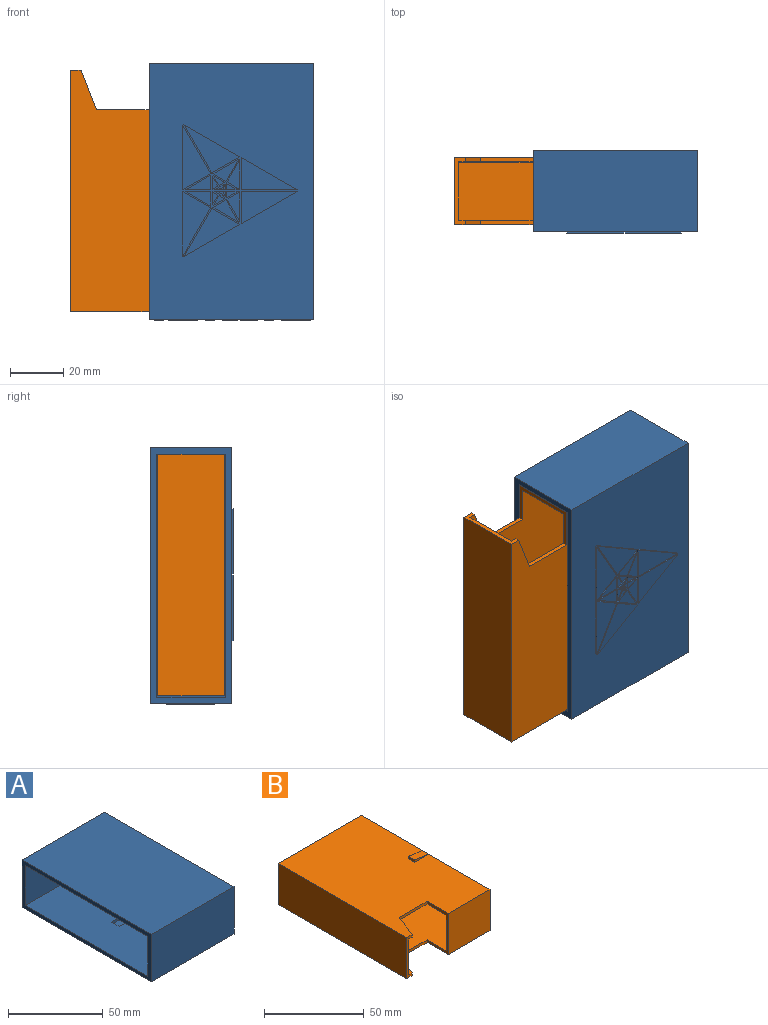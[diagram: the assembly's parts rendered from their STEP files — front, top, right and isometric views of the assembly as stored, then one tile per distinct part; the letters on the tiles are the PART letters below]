
ASSEMBLY  parts=2 mates=1
PART A: 220 faces, bbox 61.9x96.7x31.3 mm
  f0: plane 61.9x30.6mm, normal (0,1,0), area 1621.7mm2, adj f1,f2,f5,f7,f123,f124,f125,f126
  f1: plane 96.6x61.9mm, normal (0,0,-1), area 5003.8mm2, adj f0,f2,f5,f6,f27,f28,f29,f31
  f2: plane 96.6x30.6mm, normal (1,0,0), area 2577.4mm2, adj f0,f1,f6,f7,f19,f20,f21,f22
  f3: plane 91.8x59.5mm, normal (0,0,1), area 5249.3mm2, adj f5,f8,f9,f10,f15,f17,f18
  f4: plane 91.8x59.5mm, normal (0,0,-1), area 5249.3mm2, adj f5,f8,f9,f10,f11,f12,f13
  f5: plane 96.6x30.6mm, normal (-1,0,0), area 587.5mm2, adj f0,f1,f3,f4,f6,f7,f8,f9
  f6: plane 61.9x30.6mm, normal (0,-1,0), area 1894.1mm2, adj f1,f2,f5,f7
  f7: plane 96.6x61.9mm, normal (0,0,1), area 5979.5mm2, adj f0,f2,f5,f6
  f8: plane 59.5x25.8mm, normal (0,-1,0), area 1535.1mm2, adj f3,f4,f5,f10
  f9: plane 59.5x25.8mm, normal (0,1,0), area 1535.1mm2, adj f3,f4,f5,f10
  f10: plane 91.8x28.8mm, normal (-1,0,0), area 2006.7mm2, adj f3,f4,f8,f9,f11,f12,f14,f15
  f11: plane 38x1.5mm, normal (0,-1,0), area 57mm2, adj f4,f10,f13,f14
  f12: plane 38x1.5mm, normal (0,1,0), area 57mm2, adj f4,f10,f13,f14
  f13: plane 5.6x1.5mm, normal (1,0,0), area 8.4mm2, adj f4,f11,f12,f14
  f14: plane 38x5.6mm, normal (0,0,-1), area 212.8mm2, adj f10,f11,f12,f13
  f15: plane 38x1.5mm, normal (0,-1,0), area 57mm2, adj f3,f10,f16,f18
  f16: plane 38x5.6mm, normal (0,0,1), area 212.8mm2, adj f10,f15,f17,f18
  f17: plane 38x1.5mm, normal (0,1,0), area 57mm2, adj f3,f10,f16,f18
  f18: plane 5.6x1.5mm, normal (1,0,0), area 8.4mm2, adj f3,f15,f16,f17
  f19: plane 10x2.4mm, normal (0,0,1), area 24mm2, adj f2,f10,f24,f25
  f20: plane 10x2.4mm, normal (0,1,0), area 24mm2, adj f2,f10,f25,f26
  f21: plane 10x2.4mm, normal (0,0,-1), area 24mm2, adj f2,f10,f23,f26
  f22: plane 10x2.4mm, normal (0,-1,0), area 24mm2, adj f2,f10,f23,f24
  f23: cylinder r=5mm len=5mm, axis (-1,0,0), area 18.8mm2, adj f2,f10,f21,f22
  f24: cylinder r=5mm len=5mm, axis (1,0,0), area 18.8mm2, adj f2,f10,f19,f22
  f25: cylinder r=5mm len=5mm, axis (-1,0,0), area 18.8mm2, adj f2,f10,f19,f20
  f26: cylinder r=5mm len=5mm, axis (1,0,0), area 18.8mm2, adj f2,f10,f20,f21
  f27: plane 24.4x0.67mm, normal (-1,0,0), area 16.3mm2, adj f1,f28,f29,f30
  f28: plane 18.3x10.57mm, normal (0.87,0.5,0), area 14.1mm2, adj f1,f27,f29,f30
  f29: plane 10.57x6.1mm, normal (0.5,-0.87,0), area 8.1mm2, adj f1,f27,f28,f30
  f30: plane 24.4x10.57mm, normal (0,0,-1), area 128.9mm2, adj f27,f28,f29
  f31: plane 24.4x0.67mm, normal (-1,0,0), area 16.3mm2, adj f1,f32,f33,f34
  f32: plane 10.57x6.1mm, normal (0.5,0.87,0), area 8.1mm2, adj f1,f31,f33,f34
  f33: plane 18.3x10.57mm, normal (0.87,-0.5,0), area 14.1mm2, adj f1,f31,f32,f34
  f34: plane 24.4x10.57mm, normal (0,0,-1), area 128.9mm2, adj f31,f32,f33
  f35: plane 10.57x6.1mm, normal (0.5,0.87,0), area 8.1mm2, adj f1,f36,f37,f38
  f36: plane 21.13x12.2mm, normal (0.5,-0.87,0), area 16.3mm2, adj f1,f35,f37,f38
  f37: plane 18.3x10.57mm, normal (-0.87,0.5,0), area 14.1mm2, adj f1,f35,f36,f38
  f38: plane 21.13x18.3mm, normal (0,0,-1), area 128.9mm2, adj f35,f36,f37
  f39: plane 12.2x0.67mm, normal (-1,0,0), area 8.1mm2, adj f1,f40,f41,f42
  f40: plane 21.13x0.67mm, normal (0,1,0), area 14.1mm2, adj f1,f39,f41,f42
  f41: plane 21.13x12.2mm, normal (0.5,-0.87,0), area 16.3mm2, adj f1,f39,f40,f42
  f42: plane 21.13x12.2mm, normal (0,0,-1), area 128.9mm2, adj f39,f40,f41
  f43: plane 21.13x12.2mm, normal (0.5,0.87,0), area 16.3mm2, adj f1,f44,f45,f46
  f44: plane 21.13x0.67mm, normal (0,-1,0), area 14.1mm2, adj f1,f43,f45,f46
  f45: plane 12.2x0.67mm, normal (-1,0,0), area 8.1mm2, adj f1,f43,f44,f46
  f46: plane 21.13x12.2mm, normal (0,0,-1), area 128.9mm2, adj f43,f44,f45
  f47: plane 21.13x12.2mm, normal (0.5,0.87,0), area 16.3mm2, adj f1,f48,f49,f50
  f48: plane 10.57x6.1mm, normal (0.5,-0.87,0), area 8.1mm2, adj f1,f47,f49,f50
  f49: plane 18.3x10.57mm, normal (-0.87,-0.5,0), area 14.1mm2, adj f1,f47,f48,f50
  f50: plane 21.13x18.3mm, normal (0,0,-1), area 128.9mm2, adj f47,f48,f49
  f51: plane 5.62x0.67mm, normal (1,0,0), area 3.7mm2, adj f1,f52,f53,f54
  f52: plane 9.73x0.67mm, normal (0,-1,0), area 6.5mm2, adj f1,f51,f53,f54
  f53: plane 9.73x5.62mm, normal (-0.5,0.87,0), area 7.5mm2, adj f1,f51,f52,f54
  f54: plane 9.73x5.62mm, normal (0,0,-1), area 27.3mm2, adj f51,f52,f53
  f55: plane 2.47x0.67mm, normal (-1,0,0), area 1.6mm2, adj f1,f56,f57,f58
  f56: plane 4.27x2.47mm, normal (0.5,0.87,0), area 3.3mm2, adj f1,f55,f57,f58
  f57: plane 4.27x0.67mm, normal (0,-1,0), area 2.8mm2, adj f1,f55,f56,f58
  f58: plane 4.27x2.47mm, normal (0,0,-1), area 5.3mm2, adj f55,f56,f57
  f59: plane 1.7x0.98mm, normal (-0.5,0.87,0), area 1.3mm2, adj f1,f60,f61,f62
  f60: plane 0.98x0.67mm, normal (0.87,0.5,0), area 0.8mm2, adj f1,f59,f61,f62
  f61: plane 2.27x0.67mm, normal (0,-1,0), area 1.5mm2, adj f1,f59,f60,f62
  f62: plane 2.27x0.98mm, normal (0,0,-1), area 1.1mm2, adj f59,f60,f61
  f63: plane 1.14x0.67mm, normal (0,-1,0), area 0.8mm2, adj f1,f64,f65,f66
  f64: plane 1.97x1.14mm, normal (-0.87,0.5,0), area 1.5mm2, adj f1,f63,f65,f66
  f65: plane 1.97x0.67mm, normal (1,0,0), area 1.3mm2, adj f1,f63,f64,f66
  f66: plane 1.97x1.14mm, normal (0,0,-1), area 1.1mm2, adj f63,f64,f65
  f67: plane 5.62x0.67mm, normal (1,0,0), area 3.7mm2, adj f1,f68,f69,f70
  f68: plane 9.73x5.62mm, normal (-0.5,-0.87,0), area 7.5mm2, adj f1,f67,f69,f70
  f69: plane 9.73x0.67mm, normal (0,1,0), area 6.5mm2, adj f1,f67,f68,f70
  f70: plane 9.73x5.62mm, normal (0,0,-1), area 27.3mm2, adj f67,f68,f69
  f71: plane 4.27x2.47mm, normal (0.5,-0.87,0), area 3.3mm2, adj f1,f72,f73,f74
  f72: plane 2.47x0.67mm, normal (-1,0,0), area 1.6mm2, adj f1,f71,f73,f74
  f73: plane 4.27x0.67mm, normal (0,1,0), area 2.8mm2, adj f1,f71,f72,f74
  f74: plane 4.27x2.47mm, normal (0,0,-1), area 5.3mm2, adj f71,f72,f73
  f75: plane 0.98x0.67mm, normal (0.87,-0.5,0), area 0.8mm2, adj f1,f76,f77,f78
  f76: plane 1.7x0.98mm, normal (-0.5,-0.87,0), area 1.3mm2, adj f1,f75,f77,f78
  f77: plane 2.27x0.67mm, normal (0,1,0), area 1.5mm2, adj f1,f75,f76,f78
  f78: plane 2.27x0.98mm, normal (0,0,-1), area 1.1mm2, adj f75,f76,f77
  f79: plane 1.97x1.14mm, normal (-0.87,-0.5,0), area 1.5mm2, adj f1,f80,f81,f82
  f80: plane 1.14x0.67mm, normal (0,1,0), area 0.8mm2, adj f1,f79,f81,f82
  f81: plane 1.97x0.67mm, normal (1,0,0), area 1.3mm2, adj f1,f79,f80,f82
  f82: plane 1.97x1.14mm, normal (0,0,-1), area 1.1mm2, adj f79,f80,f81
  f83: plane 4.86x2.81mm, normal (-0.5,0.87,0), area 3.7mm2, adj f1,f84,f85,f86
  f84: plane 8.42x4.86mm, normal (0.87,0.5,0), area 6.5mm2, adj f1,f83,f85,f86
  f85: plane 9.73x5.62mm, normal (-0.5,-0.87,0), area 7.5mm2, adj f1,f83,f84,f86
  f86: plane 9.73x8.42mm, normal (0,0,-1), area 27.3mm2, adj f83,f84,f85
  f87: plane 4.93x0.67mm, normal (-1,0,0), area 3.3mm2, adj f1,f88,f89,f90
  f88: plane 3.7x2.14mm, normal (0.87,0.5,0), area 2.8mm2, adj f1,f87,f89,f90
  f89: plane 2.14x1.23mm, normal (0.5,-0.87,0), area 1.6mm2, adj f1,f87,f88,f90
  f90: plane 4.93x2.14mm, normal (0,0,-1), area 5.3mm2, adj f87,f88,f89
  f91: plane 0.98x0.67mm, normal (-0.87,0.5,0), area 0.8mm2, adj f1,f92,f93,f94
  f92: plane 1.97x1.14mm, normal (0.87,0.5,0), area 1.5mm2, adj f1,f91,f93,f94
  f93: plane 1.7x0.98mm, normal (-0.5,-0.87,0), area 1.3mm2, adj f1,f91,f92,f94
  f94: plane 1.97x1.7mm, normal (0,0,-1), area 1.1mm2, adj f91,f92,f93
  f95: plane 8.42x4.86mm, normal (-0.87,-0.5,0), area 6.5mm2, adj f1,f96,f97,f98
  f96: plane 4.86x2.81mm, normal (-0.5,0.87,0), area 3.7mm2, adj f1,f95,f97,f98
  f97: plane 11.23x0.67mm, normal (1,0,0), area 7.5mm2, adj f1,f95,f96,f98
  f98: plane 11.23x4.86mm, normal (0,0,-1), area 27.3mm2, adj f95,f96,f97
  f99: plane 3.7x2.14mm, normal (-0.87,-0.5,0), area 2.8mm2, adj f1,f100,f101,f102
  f100: plane 4.27x2.47mm, normal (0.5,0.87,0), area 3.3mm2, adj f1,f99,f101,f102
  f101: plane 2.14x1.23mm, normal (0.5,-0.87,0), area 1.6mm2, adj f1,f99,f100,f102
  f102: plane 4.27x3.7mm, normal (0,0,-1), area 5.3mm2, adj f99,f100,f101
  f103: plane 0.98x0.67mm, normal (-0.87,-0.5,0), area 0.8mm2, adj f1,f104,f105,f106
  f104: plane 1.7x0.98mm, normal (-0.5,0.87,0), area 1.3mm2, adj f1,f103,f105,f106
  f105: plane 1.97x1.14mm, normal (0.87,-0.5,0), area 1.5mm2, adj f1,f103,f104,f106
  f106: plane 1.97x1.7mm, normal (0,0,-1), area 1.1mm2, adj f103,f104,f105
  f107: plane 4.86x2.81mm, normal (-0.5,-0.87,0), area 3.7mm2, adj f1,f108,f109,f110
  f108: plane 8.42x4.86mm, normal (-0.87,0.5,0), area 6.5mm2, adj f1,f107,f109,f110
  f109: plane 11.23x0.67mm, normal (1,0,0), area 7.5mm2, adj f1,f107,f108,f110
  f110: plane 11.23x4.86mm, normal (0,0,-1), area 27.3mm2, adj f107,f108,f109
  f111: plane 4.27x2.47mm, normal (0.5,-0.87,0), area 3.3mm2, adj f1,f112,f113,f114
  f112: plane 3.7x2.14mm, normal (-0.87,0.5,0), area 2.8mm2, adj f1,f111,f113,f114
  f113: plane 2.14x1.23mm, normal (0.5,0.87,0), area 1.6mm2, adj f1,f111,f112,f114
  f114: plane 4.27x3.7mm, normal (0,0,-1), area 5.3mm2, adj f111,f112,f113
  f115: plane 4.86x2.81mm, normal (-0.5,-0.87,0), area 3.7mm2, adj f1,f116,f117,f118
  f116: plane 9.73x5.62mm, normal (-0.5,0.87,0), area 7.5mm2, adj f1,f115,f117,f118
  f117: plane 8.42x4.86mm, normal (0.87,-0.5,0), area 6.5mm2, adj f1,f115,f116,f118
  f118: plane 9.73x8.42mm, normal (0,0,-1), area 27.3mm2, adj f115,f116,f117
  f119: plane 3.7x2.14mm, normal (0.87,-0.5,0), area 2.8mm2, adj f1,f120,f121,f122
  f120: plane 4.93x0.67mm, normal (-1,0,0), area 3.3mm2, adj f1,f119,f121,f122
  f121: plane 2.14x1.23mm, normal (0.5,0.87,0), area 1.6mm2, adj f1,f119,f120,f122
  f122: plane 4.93x2.14mm, normal (0,0,-1), area 5.3mm2, adj f119,f120,f121
  f123: plane 13.93x0.13mm, normal (-1,0,0), area 1.8mm2, adj f0,f124,f140,f141
  f124: plane 2.96x0.13mm, normal (0,0,1), area 0.4mm2, adj f0,f123,f125,f141
  f125: plane 13.69x0.13mm, normal (1,0,0), area 1.8mm2, adj f0,f124,f126,f141
  f126: extruded ~1.69x0.81mm, area 0.3mm2, adj f0,f125,f127,f141
  f127: extruded ~2.05x0.5mm, area 0.3mm2, adj f0,f126,f128,f141
  f128: extruded ~1.09x0.13mm, area 0.1mm2, adj f0,f127,f129,f141
  f129: extruded ~1.12x0.28mm, area 0.1mm2, adj f0,f128,f130,f141
  f130: extruded ~0.98x0.34mm, area 0.1mm2, adj f0,f129,f131,f141
  f131: extruded ~0.69x0.35mm, area 0.1mm2, adj f0,f130,f132,f141
  f132: plane 1.96x1.23mm, normal (0.85,0,0.53), area 0.3mm2, adj f0,f131,f133,f141
  f133: extruded ~1.19x0.66mm, area 0.2mm2, adj f0,f132,f134,f141
  f134: extruded ~1.47x0.52mm, area 0.2mm2, adj f0,f133,f135,f141
  f135: extruded ~1.48x0.34mm, area 0.2mm2, adj f0,f134,f136,f141
  f136: extruded ~1.25x0.13mm, area 0.2mm2, adj f0,f135,f137,f141
  f137: extruded ~2.08x0.21mm, area 0.3mm2, adj f0,f136,f138,f141
  f138: extruded ~1.78x0.73mm, area 0.3mm2, adj f0,f137,f139,f141
  f139: extruded ~1.38x1.24mm, area 0.2mm2, adj f0,f138,f140,f141
  f140: extruded ~2.12x0.46mm, area 0.3mm2, adj f0,f123,f139,f141
  f141: plane 18.37x10.94mm, normal (0,1,0), area 69.8mm2, adj f123,f124,f125,f126,f127,f128,f129,f130
  f142: extruded ~1.24x0.51mm, area 0.2mm2, adj f0,f143,f149,f150
  f143: extruded ~1.23x0.51mm, area 0.2mm2, adj f0,f142,f144,f150
  f144: extruded ~1.24x0.5mm, area 0.2mm2, adj f0,f143,f145,f150
  f145: extruded ~1.21x0.5mm, area 0.2mm2, adj f0,f144,f146,f150
  f146: extruded ~1.23x0.51mm, area 0.2mm2, adj f0,f145,f147,f150
  f147: extruded ~1.24x0.5mm, area 0.2mm2, adj f0,f146,f148,f150
  f148: extruded ~1.23x0.51mm, area 0.2mm2, adj f0,f147,f149,f150
  f149: extruded ~1.24x0.51mm, area 0.2mm2, adj f0,f142,f148,f150
  f150: plane 3.47x3.47mm, normal (0,1,0), area 9.5mm2, adj f142,f143,f144,f145,f146,f147,f148,f149
  f151: extruded ~1.33x1.02mm, area 0.2mm2, adj f0,f152,f158,f159
  f152: plane 2.02x1.79mm, normal (-0.66,0,-0.75), area 0.4mm2, adj f0,f151,f153,f159
  f153: extruded ~2.26x1.46mm, area 0.4mm2, adj f0,f152,f154,f159
  f154: extruded ~2.72x0.49mm, area 0.4mm2, adj f0,f153,f155,f159
  f155: plane 0.13x0.03mm, normal (0,0,1), area 0mm2, adj f0,f154,f156,f159
  f156: plane 2.4x0.13mm, normal (1,0,0), area 0.3mm2, adj f0,f155,f157,f159
  f157: plane 0.13x0.1mm, normal (0,0,-1), area 0mm2, adj f0,f156,f158,f159
  f158: extruded ~1.56x0.32mm, area 0.2mm2, adj f0,f151,f157,f159
  f159: plane 5x3.74mm, normal (0,1,0), area 11.1mm2, adj f151,f152,f153,f154,f155,f156,f157,f158
  f160: extruded ~3.7x0.49mm, area 0.5mm2, adj f0,f161,f177,f178
  f161: extruded ~3.7x0.49mm, area 0.5mm2, adj f0,f160,f162,f178
  f162: extruded ~2.75x1.33mm, area 0.4mm2, adj f0,f161,f163,f178
  f163: extruded ~2.04x1.81mm, area 0.4mm2, adj f0,f162,f164,f178
  f164: extruded ~2.57x0.84mm, area 0.4mm2, adj f0,f163,f165,f178
  f165: plane 2.21x0.13mm, normal (-1,0,0), area 0.3mm2, adj f0,f164,f166,f178
  f166: extruded ~1.35x0.7mm, area 0.2mm2, adj f0,f165,f167,f178
  f167: extruded ~1.37x1.09mm, area 0.2mm2, adj f0,f166,f168,f178
  f168: extruded ~2.05x0.74mm, area 0.3mm2, adj f0,f167,f169,f178
  f169: extruded ~2.77x0.29mm, area 0.4mm2, adj f0,f168,f170,f178
  f170: extruded ~2.73x0.29mm, area 0.4mm2, adj f0,f169,f171,f178
  f171: extruded ~1.97x0.74mm, area 0.3mm2, adj f0,f170,f172,f178
  f172: extruded ~1.27x1.09mm, area 0.2mm2, adj f0,f171,f173,f178
  f173: extruded ~1.35x0.65mm, area 0.2mm2, adj f0,f172,f174,f178
  f174: plane 2.43x0.13mm, normal (-1,0,0), area 0.3mm2, adj f0,f173,f175,f178
  f175: extruded ~2.57x0.82mm, area 0.4mm2, adj f0,f174,f176,f178
  f176: extruded ~2.04x1.78mm, area 0.4mm2, adj f0,f175,f177,f178
  f177: extruded ~2.74x1.33mm, area 0.4mm2, adj f0,f160,f176,f178
  f178: plane 18.15x6.43mm, normal (0,1,0), area 55.8mm2, adj f160,f161,f162,f163,f164,f165,f166,f167
  f179: plane 6.91x0.13mm, normal (-1,0,0), area 0.9mm2, adj f0,f180,f193,f194
  f180: plane 5.92x0.13mm, normal (0,0,1), area 0.8mm2, adj f0,f179,f181,f194
  f181: plane 1.99x0.13mm, normal (1,0,0), area 0.3mm2, adj f0,f180,f182,f194
  f182: plane 3.04x0.13mm, normal (0,0,-1), area 0.4mm2, adj f0,f181,f183,f194
  f183: plane 4.42x0.13mm, normal (1,0,0), area 0.6mm2, adj f0,f182,f184,f194
  f184: extruded ~0.6x0.41mm, area 0.1mm2, adj f0,f183,f185,f194
  f185: extruded ~0.85x0.23mm, area 0.1mm2, adj f0,f184,f186,f194
  f186: extruded ~0.87x0.13mm, area 0.1mm2, adj f0,f185,f187,f194
  f187: extruded ~0.72x0.13mm, area 0.1mm2, adj f0,f186,f188,f194
  f188: plane 2.14x0.13mm, normal (1,0,0), area 0.3mm2, adj f0,f187,f189,f194
  f189: plane 0.13x0.03mm, normal (0,0,-1), area 0mm2, adj f0,f188,f190,f194
  f190: extruded ~1.61x0.13mm, area 0.2mm2, adj f0,f189,f191,f194
  f191: extruded ~1.58x0.41mm, area 0.2mm2, adj f0,f190,f192,f194
  f192: extruded ~1.46x0.74mm, area 0.2mm2, adj f0,f191,f193,f194
  f193: extruded ~1.25x1.15mm, area 0.2mm2, adj f0,f179,f192,f194
  f194: plane 9.34x5.92mm, normal (0,1,0), area 36.1mm2, adj f179,f180,f181,f182,f183,f184,f185,f186
  f195: extruded ~1.24x0.51mm, area 0.2mm2, adj f0,f196,f202,f203
  f196: extruded ~1.23x0.51mm, area 0.2mm2, adj f0,f195,f197,f203
  f197: extruded ~1.24x0.5mm, area 0.2mm2, adj f0,f196,f198,f203
  f198: extruded ~1.21x0.5mm, area 0.2mm2, adj f0,f197,f199,f203
  f199: extruded ~1.23x0.51mm, area 0.2mm2, adj f0,f198,f200,f203
  f200: extruded ~1.24x0.5mm, area 0.2mm2, adj f0,f199,f201,f203
  f201: extruded ~1.23x0.51mm, area 0.2mm2, adj f0,f200,f202,f203
  f202: extruded ~1.24x0.51mm, area 0.2mm2, adj f0,f195,f201,f203
  f203: plane 3.47x3.47mm, normal (0,1,0), area 9.5mm2, adj f195,f196,f197,f198,f199,f200,f201,f202
  f204: plane 15.67x0.13mm, normal (-1,0,0), area 2mm2, adj f0,f205,f209,f210
  f205: plane 2.96x0.13mm, normal (0,0,1), area 0.4mm2, adj f0,f204,f206,f210
  f206: plane 17.88x0.13mm, normal (1,0,0), area 2.3mm2, adj f0,f205,f207,f210
  f207: plane 11.19x0.13mm, normal (0,0,-1), area 1.5mm2, adj f0,f206,f208,f210
  f208: plane 2.21x0.13mm, normal (-1,0,0), area 0.3mm2, adj f0,f207,f209,f210
  f209: plane 8.23x0.13mm, normal (0,0,1), area 1.1mm2, adj f0,f204,f208,f210
  f210: plane 17.88x11.19mm, normal (0,1,0), area 71.1mm2, adj f204,f205,f206,f207,f208,f209
  f211: extruded ~1.24x0.51mm, area 0.2mm2, adj f0,f212,f218,f219
  f212: extruded ~1.23x0.51mm, area 0.2mm2, adj f0,f211,f213,f219
  f213: extruded ~1.24x0.5mm, area 0.2mm2, adj f0,f212,f214,f219
  f214: extruded ~1.21x0.5mm, area 0.2mm2, adj f0,f213,f215,f219
  f215: extruded ~1.23x0.51mm, area 0.2mm2, adj f0,f214,f216,f219
  f216: extruded ~1.24x0.5mm, area 0.2mm2, adj f0,f215,f217,f219
  f217: extruded ~1.23x0.51mm, area 0.2mm2, adj f0,f216,f218,f219
  f218: extruded ~1.24x0.51mm, area 0.2mm2, adj f0,f211,f217,f219
  f219: plane 3.47x3.47mm, normal (0,1,0), area 9.5mm2, adj f211,f212,f213,f214,f215,f216,f217,f218
PART B: 26 faces, bbox 59.2x91.2x28.2 mm
  f0: plane 91.2x59.2mm, normal (0,0,-1), area 5014.2mm2, adj f8,f10,f11,f12,f13,f14,f15,f16
  f1: plane 15x5.76mm, normal (0.93,-0.36,0), area 25.7mm2, adj f6,f9,f13,f17
  f2: plane 28x22mm, normal (0,1,0), area 616mm2, adj f3,f6,f7,f8
  f3: plane 88x22mm, normal (-1,0,0), area 1936mm2, adj f2,f4,f6,f7
  f4: plane 56x22mm, normal (0,-1,0), area 1232mm2, adj f3,f5,f6,f7
  f5: plane 89.6x22mm, normal (1,0,0), area 1971.2mm2, adj f4,f6,f7,f13
  f6: plane 89.6x56mm, normal (0,0,-1), area 4632mm2, adj f1,f2,f3,f4,f5,f8,f9,f13
  f7: plane 89.6x56mm, normal (0,0,1), area 4632mm2, adj f2,f3,f4,f5,f8,f10,f11,f13
  f8: plane 25.2x15mm, normal (-1,0,0), area 83.2mm2, adj f0,f2,f6,f7,f9,f11,f12,f17
  f9: plane 19.84x1.6mm, normal (0,-1,0), area 31.7mm2, adj f1,f6,f8,f17
  f10: plane 15x5.76mm, normal (0.93,-0.36,0), area 25.7mm2, adj f0,f7,f11,f13
  f11: plane 19.84x1.6mm, normal (0,-1,0), area 31.7mm2, adj f0,f7,f8,f10
  f12: plane 29.6x25.2mm, normal (0,-1,0), area 745.9mm2, adj f0,f8,f14,f17
  f13: plane 25.2x4mm, normal (0,-1,0), area 48mm2, adj f0,f1,f5,f6,f7,f10,f16,f17
  f14: plane 91.2x25.21mm, normal (1,0,0), area 2298.3mm2, adj f0,f12,f15,f17,f18,f19,f20,f22
  f15: plane 59.2x25.2mm, normal (0,1,0), area 1491.8mm2, adj f0,f14,f16,f17
  f16: plane 91.2x25.2mm, normal (-1,0,0), area 2298.2mm2, adj f0,f13,f15,f17
  f17: plane 91.2x59.2mm, normal (0,0,1), area 5014.2mm2, adj f1,f8,f9,f12,f13,f14,f15,f16
  f18: plane 10x1.5mm, normal (0,-1,0), area 7.5mm2, adj f0,f14,f19,f21
  f19: plane 10x4.4mm, normal (0.15,0,-0.99), area 44.5mm2, adj f14,f18,f20,f21
  f20: plane 10x1.5mm, normal (0,1,0), area 7.5mm2, adj f0,f14,f19,f21
  f21: plane 4.4x1.5mm, normal (-1,0,0), area 6.6mm2, adj f0,f18,f19,f20
  f22: plane 10x1.5mm, normal (0,1,0), area 7.5mm2, adj f14,f17,f23,f25
  f23: plane 10x4.4mm, normal (0.15,0,0.99), area 44.5mm2, adj f14,f22,f24,f25
  f24: plane 10x1.5mm, normal (0,-1,0), area 7.5mm2, adj f14,f17,f23,f25
  f25: plane 4.4x1.5mm, normal (-1,0,0), area 6.6mm2, adj f17,f22,f23,f24
PLACE A rot(axis=(-1,0,0),90deg) t=(-48.05,18.61,-0.4)mm
PLACE B rot(axis=(-1,0,0),90deg) t=(-77.75,-11.99,-0.1)mm
MATE slider A.f10 <-> B.f14  axis (-1,0,0) through (-18.15,0.61,45.5)mm
